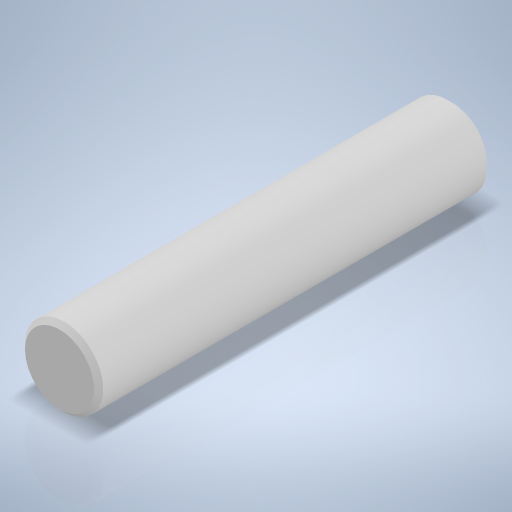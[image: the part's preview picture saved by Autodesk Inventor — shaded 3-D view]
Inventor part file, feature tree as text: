
AUTODESK INVENTOR PART (.ipt)
format: ipt  version: 2024 (Build 280153000, 153)  size: 231,936 bytes
history: native  units: mm
features: extrude x1, chamfer x1, sketch x1
ambient origin geometry x8: Origin, YZ Plane, XZ Plane, XY Plane, X Axis, Y Axis, Z Axis, Center Point
bodies: Volumenkörper1 (feature_tree)
feature tree (3):
  extrude  "Extrusion1"  Depth=30.0mm TaperAngle=0.0deg
  chamfer  "Fasen1"  Distance=0.35mm Angle=45.0deg
  sketch  "Skizze1"  dims[d0=5.98mm d1=30.0mm d2=0.0mm d3=0.35mm d4=2.0mm d5=45.0deg]
